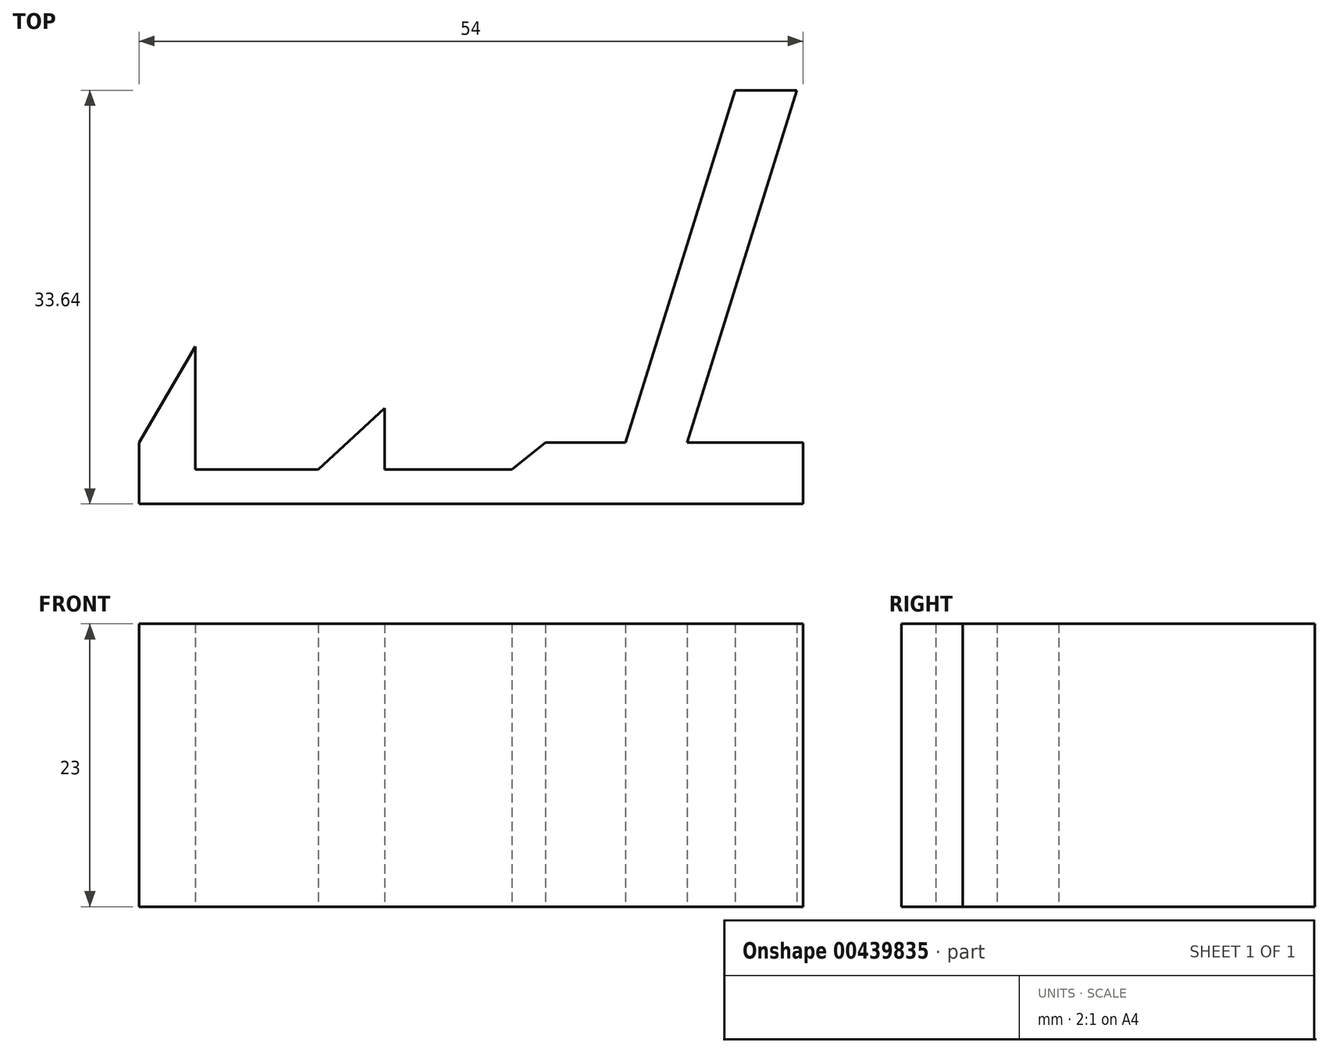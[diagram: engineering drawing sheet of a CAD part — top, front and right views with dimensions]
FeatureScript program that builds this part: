
annotation { "Feature Type Name" : "Feature", "Feature Type Description" : "" }
export const myFeature = defineFeature(function(context is Context, id is Id, definition is map)
    precondition{}
    {
        {
            var Q0;
            Q0=qCreatedBy(makeId("Top.planeOp"),FACE);
            var sketch = newSketch(context, id + "F0", { "sketchPlane" : qUnion([Q0])});
            skLineSegment(sketch, "E0.top", {"start": v(-27, -2.8) * mm, "end": v(27, -2.8) * mm});
            skLineSegment(sketch, "E0.right", {"start": v(27, 2.2) * mm, "end": v(27, -2.8) * mm});
            skLineSegment(sketch, "E1.MirrorCS", {"start": v(-27, 2.2) * mm, "end": v(-27, -2.8) * mm});
            skLineSegment(sketch, "E2", {"start": v(17.57, 2.2) * mm, "end": v(26.49, 30.85) * mm});
            skLineSegment(sketch, "E3", {"start": v(26.49, 30.85) * mm, "end": v(21.49, 30.85) * mm});
            skLineSegment(sketch, "E4", {"start": v(21.49, 30.85) * mm, "end": v(12.57, 2.2) * mm});
            skLineSegment(sketch, "E5", {"start": v(-6.68, 0) * mm, "end": v(3.32, 0) * mm});
            skLineSegment(sketch, "E6", {"start": v(3.32, 0) * mm, "end": v(6.05, 2.2) * mm});
            skLineSegment(sketch, "E7.trimOffspring", {"start": v(6.05, 2.2) * mm, "end": v(27, 2.2) * mm});
            skLineSegment(sketch, "E8", {"start": v(-27, 2.2) * mm, "end": v(-22.44, 10) * mm});
            skLineSegment(sketch, "E9", {"start": v(-22.44, 10) * mm, "end": v(-22.44, 0) * mm});
            skLineSegment(sketch, "E10", {"start": v(-22.44, 0) * mm, "end": v(-12.44, 0) * mm});
            skLineSegment(sketch, "E11", {"start": v(-12.44, 0) * mm, "end": v(-7.03, 5) * mm});
            skLineSegment(sketch, "E12", {"start": v(-7.03, 5) * mm, "end": v(-7.03, 0) * mm});
            skLineSegment(sketch, "E13", {"start": v(3.32, 0) * mm, "end": v(-7.03, 0) * mm});
            skSolve(sketch);
        }
        {
            var Q0;
            Q0=makeQuery(id+"F0.imprint","IMPRINT",FACE,{"disambiguationData":[TD([[makeQuery(id+"F0.imprint","IMPRINT",EDGE,{"derivedFrom":sQuery(id+"F0.wireOp",EDGE,"E0.top")}),1.0]])]});
            var Q1;
            {var subQ0=sQuery(id+"F0.wireOp",EDGE,"E2");Q1=makeQuery(id+"F0.imprint","IMPRINT",FACE,{"disambiguationData":[TD([[makeQuery(id+"F0.imprint","IMPRINT",EDGE,{"derivedFrom":subQ0}),1.0]])]});}
            extrude(context, id + "F1", {"entities" : qUnion([Q0, Q1]), "depth" : 23 * mm});
        }
    });
